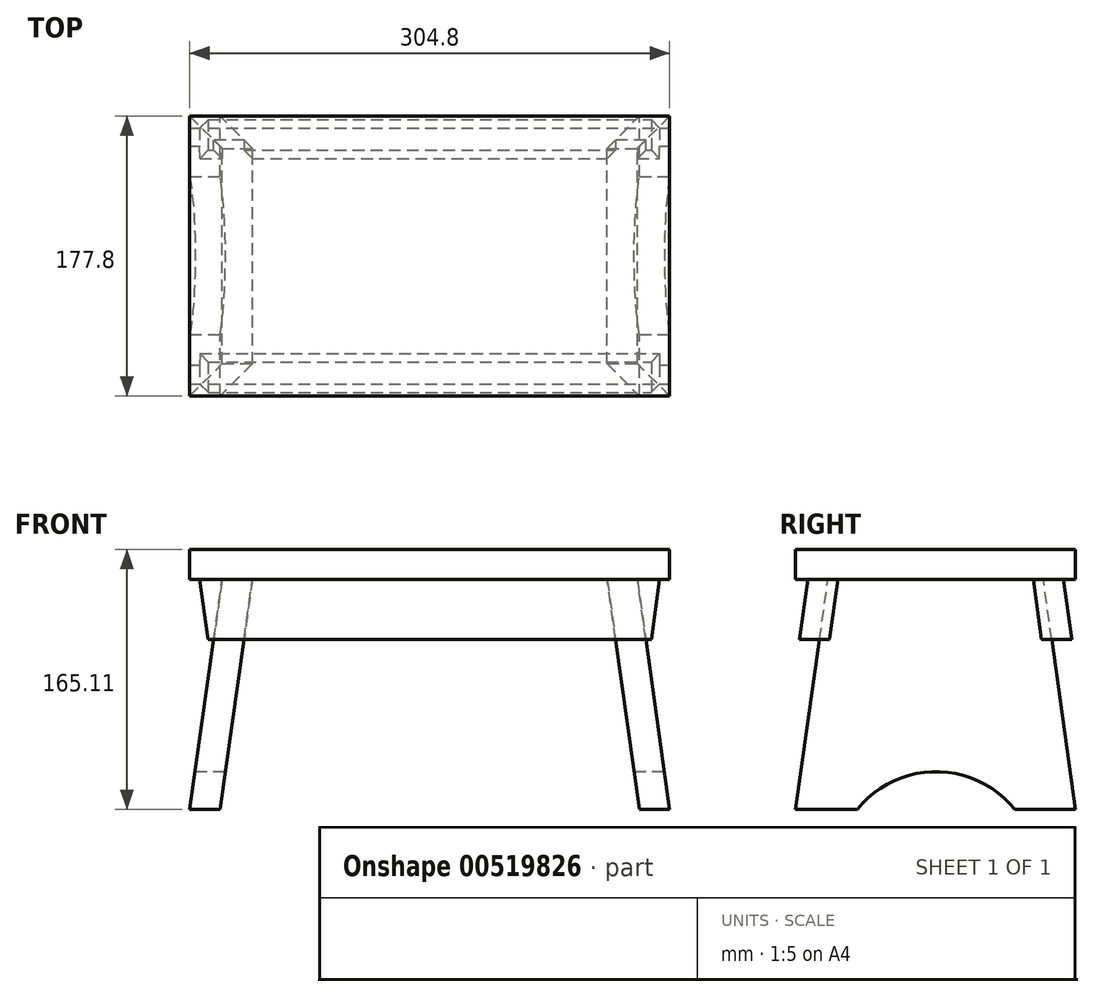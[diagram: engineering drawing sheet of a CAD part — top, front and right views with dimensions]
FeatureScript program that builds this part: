
annotation { "Feature Type Name" : "Feature", "Feature Type Description" : "" }
export const myFeature = defineFeature(function(context is Context, id is Id, definition is map)
    precondition{}
    {
        {
            var Q0;
            Q0=qCreatedBy(makeId("Front.planeOp"),FACE);
            var sketch = newSketch(context, id + "F0", { "sketchPlane" : qUnion([Q0])});
            skLineSegment(sketch, "E0.bottom", {"start": v(-152.4, 9.53) * mm, "end": v(152.4, 9.53) * mm});
            skLineSegment(sketch, "E0.top", {"start": v(-152.4, -9.52) * mm, "end": v(152.4, -9.52) * mm});
            skLineSegment(sketch, "E0.left", {"start": v(-152.4, 9.53) * mm, "end": v(-152.4, -9.52) * mm});
            skLineSegment(sketch, "E0.right", {"start": v(152.4, 9.53) * mm, "end": v(152.4, -9.52) * mm});
            skPoint(sketch, "E0.middle", {"position": v(0, 0) * mm});
            skLineSegment(sketch, "E1.bottom", {"start": v(-152.4, -9.52) * mm, "end": v(146.05, -9.52) * mm, "construction": true});
            skLineSegment(sketch, "E1.top", {"start": v(-152.4, -155.57) * mm, "end": v(152.4, -155.57) * mm, "construction": true});
            skLineSegment(sketch, "E1.left", {"start": v(-152.4, -9.52) * mm, "end": v(-152.4, -155.57) * mm, "construction": true});
            skLineSegment(sketch, "E1.right", {"start": v(152.4, -9.52) * mm, "end": v(152.4, -155.57) * mm, "construction": true});
            skLineSegment(sketch, "E2", {"start": v(131.87, -9.52) * mm, "end": v(152.4, -155.57) * mm});
            skLineSegment(sketch, "E3", {"start": v(152.4, -155.57) * mm, "end": v(133.16, -155.57) * mm});
            skLineSegment(sketch, "E4", {"start": v(133.16, -155.57) * mm, "end": v(112.64, -9.52) * mm});
            skLineSegment(sketch, "E5", {"start": v(112.64, -9.52) * mm, "end": v(131.87, -9.52) * mm});
            skLineSegment(sketch, "E6", {"start": v(0, 0) * mm, "end": v(0, -155.57) * mm, "construction": true});
            skLineSegment(sketch, "E7.MirrorCS", {"start": v(-112.64, -9.52) * mm, "end": v(-131.87, -9.52) * mm});
            skLineSegment(sketch, "E8.MirrorCS", {"start": v(-133.16, -155.57) * mm, "end": v(-112.64, -9.52) * mm});
            skLineSegment(sketch, "E9.MirrorCS", {"start": v(-152.4, -155.57) * mm, "end": v(-133.16, -155.57) * mm});
            skLineSegment(sketch, "E10.MirrorCS", {"start": v(-131.87, -9.52) * mm, "end": v(-152.4, -155.57) * mm});
            skLineSegment(sketch, "E11.bottom", {"start": v(-152.4, -9.52) * mm, "end": v(146.05, -9.52) * mm});
            skLineSegment(sketch, "E11.top", {"start": v(-152.4, -47.62) * mm, "end": v(152.4, -47.62) * mm});
            skLineSegment(sketch, "E11.left", {"start": v(-152.4, -9.52) * mm, "end": v(-152.4, -47.62) * mm});
            skLineSegment(sketch, "E11.right", {"start": v(152.4, -9.52) * mm, "end": v(152.4, -47.62) * mm});
            skLineSegment(sketch, "E12.MirrorCS", {"start": v(146.05, -9.52) * mm, "end": v(140.7, -47.62) * mm});
            skLineSegment(sketch, "E13.MirrorCS", {"start": v(-146.05, -9.52) * mm, "end": v(-140.7, -47.62) * mm});
            skSolve(sketch);
        }
        {
            var Q0;
            Q0=makeQuery(id+"F0.imprint","IMPRINT",FACE,{"disambiguationData":[TD([[makeQuery(id+"F0.imprint","IMPRINT",EDGE,{"derivedFrom":sQuery(id+"F0.wireOp",EDGE,"E0.bottom")}),-1.0]])]});
            extrude(context, id + "F1", {"entities" : qUnion([Q0]), "endBound" : BoundingType.SYMMETRIC, "depth" : 177.8 * mm, "offsetDistance" : 25.4 * mm});
        }
        {
            var Q0;
            {var subQ0=sQuery(id+"F0.wireOp",EDGE,"E9.MirrorCS");Q0=makeQuery(id+"F0.imprint","IMPRINT",FACE,{"disambiguationData":[TD([[makeQuery(id+"F0.imprint","IMPRINT",EDGE,{"derivedFrom":subQ0}),1.0]])]});}
            var Q1;
            {var subQ0=sQuery(id+"F0.wireOp",EDGE,"E3");Q1=makeQuery(id+"F0.imprint","IMPRINT",FACE,{"disambiguationData":[TD([[makeQuery(id+"F0.imprint","IMPRINT",EDGE,{"derivedFrom":subQ0}),-1.0]])]});}
            var Q2;
            {var subQ0=sQuery(id+"F0.wireOp",EDGE,"E11.bottom");var subQ1=sQuery(id+"F0.wireOp",EDGE,"E2");var subQ2=makeQuery(id+"F0.imprint","INTERSECT",VERTEX,{"derivedFrom":[subQ1,subQ0]});Q2=makeQuery(id+"F0.imprint","IMPRINT",FACE,{"disambiguationData":[TD([[makeQuery(id+"F0.imprint","IMPRINT",EDGE,{"disambiguationData":[TD([[subQ2,-1.0]])],"derivedFrom":subQ1}),-1.0]])]});}
            var Q3;
            {var subQ0=sQuery(id+"F0.wireOp",EDGE,"E11.bottom");var subQ1=sQuery(id+"F0.wireOp",EDGE,"E8.MirrorCS");var subQ2=makeQuery(id+"F0.imprint","INTERSECT",VERTEX,{"derivedFrom":[subQ1,subQ0]});Q3=makeQuery(id+"F0.imprint","IMPRINT",FACE,{"disambiguationData":[TD([[makeQuery(id+"F0.imprint","IMPRINT",EDGE,{"disambiguationData":[TD([[subQ2,1.0]])],"derivedFrom":subQ1}),1.0]])]});}
            var Q4;
            Q4=makeQuery(id+"F1.opExtrude","CAP_VERTEX",VERTEX,{"disambiguationData":[OSD([sQuery(id+"F0.wireOp",EDGE,"E0.right"),sQuery(id+"F0.wireOp",EDGE,"E11.bottom"),sQuery(id+"F0.wireOp",EDGE,"E11.right")])],"isStart":false});
            var Q5;
            Q5=makeQuery(id+"F1.opExtrude","CAP_VERTEX",VERTEX,{"disambiguationData":[OSD([sQuery(id+"F0.wireOp",EDGE,"E0.right"),sQuery(id+"F0.wireOp",EDGE,"E11.bottom"),sQuery(id+"F0.wireOp",EDGE,"E11.right")])],"isStart":true});
            extrude(context, id + "F2", {"entities" : qUnion([Q0, Q1, Q2, Q3]), "endBound" : BoundingType.UP_TO_VERTEX, "depth" : 25.4 * mm, "endBoundEntityVertex" : qUnion([Q4]), "offsetDistance" : 25.4 * mm, "hasSecondDirection" : true, "secondDirectionBound" : SecondDirectionBoundingType.UP_TO_VERTEX, "secondDirectionOppositeDirection" : true, "secondDirectionDepth" : 25.4 * mm, "secondDirectionBoundEntityVertex" : qUnion([Q5])});
        }
        {
            var Q0;
            Q0=qCreatedBy(makeId("Right.planeOp"),FACE);
            var sketch = newSketch(context, id + "F3", { "sketchPlane" : qUnion([Q0])});
            skLineSegment(sketch, "E14.0.0", {"start": v(88.9, -9.52) * mm, "end": v(-88.9, -9.52) * mm});
            skLineSegment(sketch, "E14.0.1", {"start": v(-88.9, -9.52) * mm, "end": v(-88.9, -155.57) * mm});
            skLineSegment(sketch, "E14.0.2", {"start": v(-88.9, -155.57) * mm, "end": v(88.9, -155.57) * mm});
            skLineSegment(sketch, "E14.0.3", {"start": v(88.9, -155.57) * mm, "end": v(88.9, -9.52) * mm});
            skLineSegment(sketch, "E15", {"start": v(-88.9, -155.57) * mm, "end": v(-68.37, -9.53) * mm});
            skLineSegment(sketch, "E16.MirrorCS", {"start": v(88.9, -155.57) * mm, "end": v(68.37, -9.53) * mm});
            skArc(sketch, "E17", {"start": v(50.36, -155.57) * mm, "mid": v(0.28, -131.5) * mm, "end": v(-49.81, -155.57) * mm});
            skSolve(sketch);
        }
        {
            var Q0;
            {var subQ0=sQuery(id+"F3.wireOp",EDGE,"E14.0.1");Q0=makeQuery(id+"F3.imprint","IMPRINT",FACE,{"disambiguationData":[TD([[makeQuery(id+"F3.imprint","IMPRINT",EDGE,{"derivedFrom":subQ0}),1.0]])]});}
            var Q1;
            {var subQ0=sQuery(id+"F3.wireOp",EDGE,"fWZCDtoD-VZHa-qSUP-SHpk-wquZ9ZQm2nNB");Q1=makeQuery(id+"F3.imprint","IMPRINT",FACE,{"disambiguationData":[TD([[makeQuery(id+"F3.imprint","IMPRINT",EDGE,{"derivedFrom":subQ0}),1.0]])]});}
            var Q2;
            {var subQ0=sQuery(id+"F3.wireOp",EDGE,"E14.0.3");Q2=makeQuery(id+"F3.imprint","IMPRINT",FACE,{"disambiguationData":[TD([[makeQuery(id+"F3.imprint","IMPRINT",EDGE,{"derivedFrom":subQ0}),1.0]])]});}
            var Q3;
            {var subQ0=sQuery(id+"F3.wireOp",EDGE,"E17");Q3=makeQuery(id+"F3.imprint","IMPRINT",FACE,{"disambiguationData":[TD([[makeQuery(id+"F3.imprint","IMPRINT",EDGE,{"derivedFrom":subQ0}),1.0]])]});}
            extrude(context, id + "F4", {"entities" : qUnion([Q0, Q1, Q2, Q3]), "operationType" : NewBodyOperationType.REMOVE, "endBound" : BoundingType.THROUGH_ALL, "oppositeDirection" : true, "depth" : 201.93 * mm, "offsetDistance" : 25.4 * mm, "hasSecondDirection" : true, "secondDirectionBound" : SecondDirectionBoundingType.THROUGH_ALL, "secondDirectionOppositeDirection" : false, "secondDirectionDepth" : 25.4 * mm});
        }
        {
            var Q0;
            Q0=qCreatedBy(makeId("Right.planeOp"),FACE);
            var sketch = newSketch(context, id + "F5", { "sketchPlane" : qUnion([Q0])});
            skLineSegment(sketch, "E18.0", {"start": v(-68.37, -9.53) * mm, "end": v(-88.9, -155.58) * mm});
            skLineSegment(sketch, "E19.0", {"start": v(68.37, -9.52) * mm, "end": v(88.9, -155.57) * mm});
            skLineSegment(sketch, "E20.MirrorCS", {"start": v(61.97, -9.58) * mm, "end": v(81.19, -9.44) * mm});
            skLineSegment(sketch, "E21.MirrorCS", {"start": v(67.32, -47.62) * mm, "end": v(61.97, -9.58) * mm});
            skLineSegment(sketch, "E22.MirrorCS", {"start": v(81.19, -9.44) * mm, "end": v(86.55, -47.62) * mm});
            skLineSegment(sketch, "E23.MirrorCS", {"start": v(86.55, -47.62) * mm, "end": v(67.32, -47.62) * mm});
            skLineSegment(sketch, "E24.MirrorCS", {"start": v(-81.19, -9.44) * mm, "end": v(-86.55, -47.62) * mm});
            skLineSegment(sketch, "E25.MirrorCS", {"start": v(-67.32, -47.62) * mm, "end": v(-61.97, -9.58) * mm});
            skLineSegment(sketch, "E26.MirrorCS", {"start": v(-86.55, -47.62) * mm, "end": v(-67.32, -47.62) * mm});
            skLineSegment(sketch, "E27.MirrorCS", {"start": v(-61.97, -9.58) * mm, "end": v(-81.19, -9.44) * mm});
            skSolve(sketch);
        }
        {
            var Q0;
            {var subQ5=sQuery(id+"F5.wireOp",EDGE,"E21.MirrorCS");Q0=makeQuery(id+"F5.imprint","IMPRINT",FACE,{"disambiguationData":[TD([[makeQuery(id+"F5.imprint","IMPRINT",EDGE,{"derivedFrom":subQ5}),-1.0]])]});}
            var Q1;
            {var subQ5=sQuery(id+"F5.wireOp",EDGE,"E24.MirrorCS");Q1=makeQuery(id+"F5.imprint","IMPRINT",FACE,{"disambiguationData":[TD([[makeQuery(id+"F5.imprint","IMPRINT",EDGE,{"derivedFrom":subQ5}),1.0]])]});}
            var Q2;
            {var subQ5=sQuery(id+"F5.wireOp",EDGE,"E25.MirrorCS");Q2=makeQuery(id+"F5.imprint","IMPRINT",FACE,{"disambiguationData":[TD([[makeQuery(id+"F5.imprint","IMPRINT",EDGE,{"derivedFrom":subQ5}),1.0]])]});}
            var Q3;
            {var subQ5=sQuery(id+"F5.wireOp",EDGE,"E22.MirrorCS");Q3=makeQuery(id+"F5.imprint","IMPRINT",FACE,{"disambiguationData":[TD([[makeQuery(id+"F5.imprint","IMPRINT",EDGE,{"derivedFrom":subQ5}),-1.0]])]});}
            var Q4;
            Q4=makeQuery(id+"F1.opExtrude","SWEPT_FACE",FACE,{"disambiguationData":[OSD([sQuery(id+"F0.wireOp",EDGE,"E0.left")])]});
            var Q5;
            Q5=makeQuery(id+"F1.opExtrude","SWEPT_FACE",FACE,{"disambiguationData":[OSD([sQuery(id+"F0.wireOp",EDGE,"E0.right")])]});
            extrude(context, id + "F6", {"entities" : qUnion([Q0, Q1, Q2, Q3]), "endBound" : BoundingType.UP_TO_SURFACE, "oppositeDirection" : true, "depth" : 25.4 * mm, "endBoundEntityFace" : qUnion([Q4]), "offsetDistance" : 25.4 * mm, "hasSecondDirection" : true, "secondDirectionBound" : SecondDirectionBoundingType.UP_TO_SURFACE, "secondDirectionOppositeDirection" : false, "secondDirectionDepth" : 25.4 * mm, "secondDirectionBoundEntityFace" : qUnion([Q5])});
        }
        {
            var Q0;
            {var subQ0=sQuery(id+"F0.wireOp",EDGE,"E11.right");Q0=makeQuery(id+"F0.imprint","IMPRINT",FACE,{"disambiguationData":[TD([[makeQuery(id+"F0.imprint","IMPRINT",EDGE,{"derivedFrom":subQ0}),-1.0]])]});}
            var Q1;
            {var subQ0=sQuery(id+"F0.wireOp",EDGE,"E11.left");Q1=makeQuery(id+"F0.imprint","IMPRINT",FACE,{"disambiguationData":[TD([[makeQuery(id+"F0.imprint","IMPRINT",EDGE,{"derivedFrom":subQ0}),1.0]])]});}
            extrude(context, id + "F7", {"entities" : qUnion([Q0, Q1]), "operationType" : NewBodyOperationType.REMOVE, "endBound" : BoundingType.THROUGH_ALL, "oppositeDirection" : true, "depth" : 25.4 * mm, "offsetDistance" : 25.4 * mm, "hasSecondDirection" : true, "secondDirectionBound" : SecondDirectionBoundingType.THROUGH_ALL, "secondDirectionOppositeDirection" : false, "secondDirectionDepth" : 25.4 * mm});
        }
        {
            var Q0;
            Q0=makeQuery(id+"F2.opExtrude","SWEPT_BODY",BODY,{"disambiguationData":[OSD([sQuery(id+"F0.wireOp",EDGE,"E8.MirrorCS"),sQuery(id+"F0.wireOp",EDGE,"E9.MirrorCS"),sQuery(id+"F0.wireOp",EDGE,"E10.MirrorCS"),sQuery(id+"F0.wireOp",EDGE,"E11.bottom")])]});
            var Q1;
            Q1=makeQuery(id+"F2.opExtrude","SWEPT_BODY",BODY,{"disambiguationData":[OSD([sQuery(id+"F0.wireOp",EDGE,"E2"),sQuery(id+"F0.wireOp",EDGE,"E3"),sQuery(id+"F0.wireOp",EDGE,"E4"),sQuery(id+"F0.wireOp",EDGE,"E11.bottom")])]});
            var Q2;
            Q2=makeQuery(id+"F6.opExtrude","SWEPT_BODY",BODY,{"disambiguationData":[OSD([sQuery(id+"F5.wireOp",EDGE,"rTdEhVsn-Y1tV-qdTK-qoAY-RtYbIHnJSGx4"),sQuery(id+"F5.wireOp",EDGE,"9hM1NdmH-Pkbj-aHXD-XwvQ-aR5TofK7t3gS"),sQuery(id+"F5.wireOp",EDGE,"zxE2qgf0-YAUP-Etyz-C7p6-nTIKVjYCknYT"),sQuery(id+"F5.wireOp",EDGE,"3tRp82C4-5P3i-FWgb-zm2X-qLotrktaonv7")])]});
            var Q3;
            Q3=makeQuery(id+"F6.opExtrude","SWEPT_BODY",BODY,{"disambiguationData":[OSD([sQuery(id+"F5.wireOp",EDGE,"E20.MirrorCS"),sQuery(id+"F5.wireOp",EDGE,"E21.MirrorCS"),sQuery(id+"F5.wireOp",EDGE,"E22.MirrorCS"),sQuery(id+"F5.wireOp",EDGE,"E23.MirrorCS")])]});
            booleanBodies(context, id + "F8", {"operationType" : BooleanOperationType.SUBTRACTION, "tools" : qUnion([Q0, Q1]), "targets" : qUnion([Q2, Q3]), "keepTools" : true});
        }
    });
